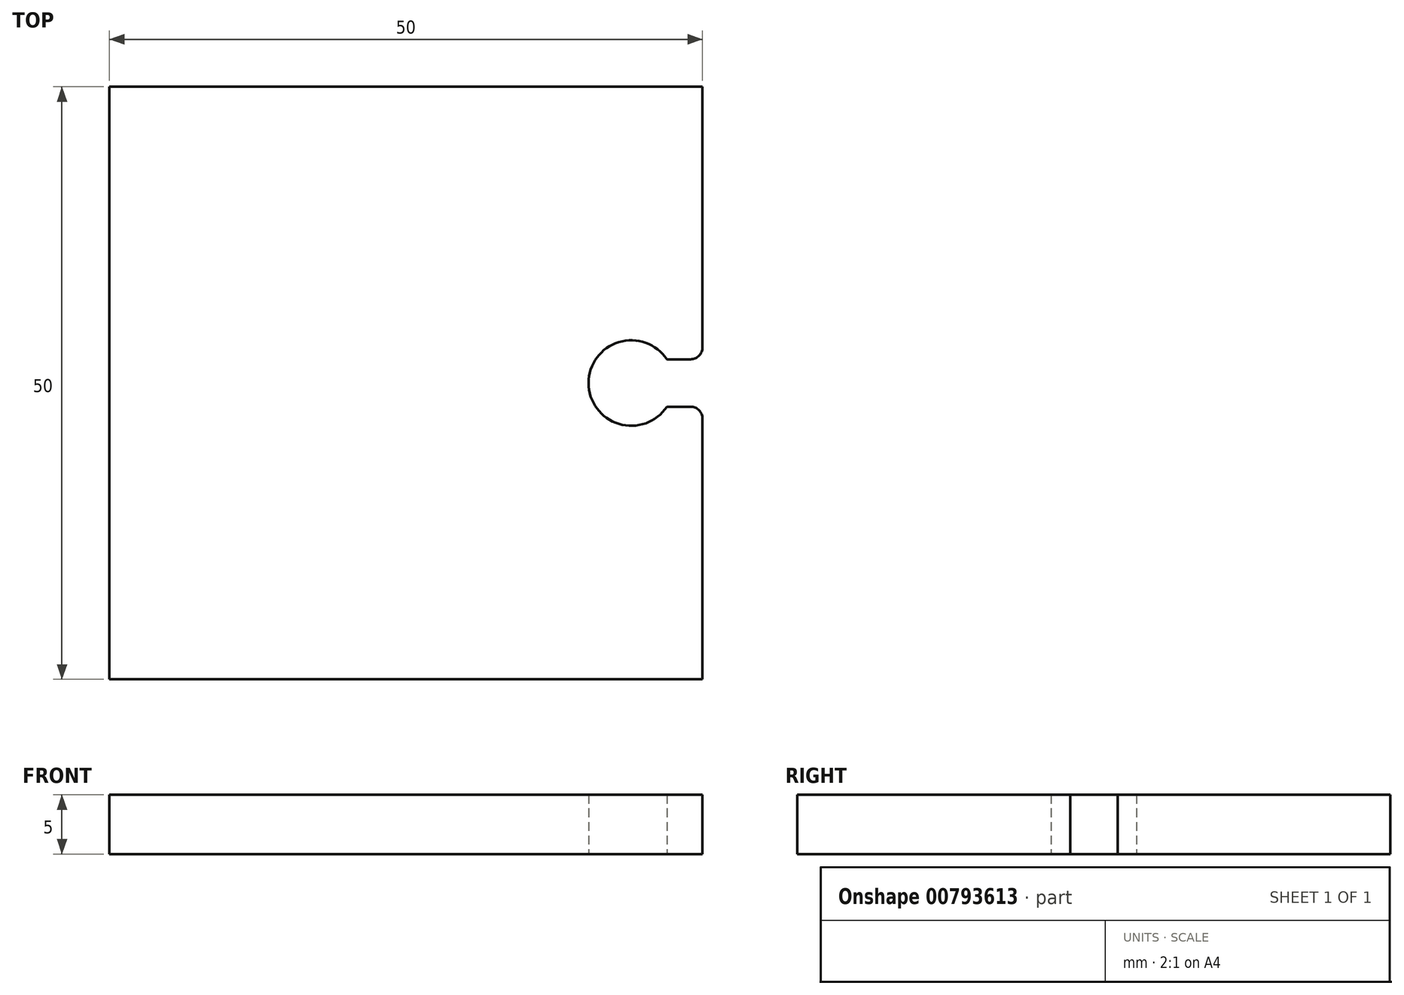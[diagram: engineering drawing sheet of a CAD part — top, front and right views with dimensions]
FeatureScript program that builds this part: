
annotation { "Feature Type Name" : "Feature", "Feature Type Description" : "" }
export const myFeature = defineFeature(function(context is Context, id is Id, definition is map)
    precondition{}
    {
        {
            var Q0;
            Q0=qCreatedBy(makeId("Top.planeOp"),FACE);
            var sketch = newSketch(context, id + "F0", { "sketchPlane" : qUnion([Q0])});
            skLineSegment(sketch, "E0.bottom", {"start": v(-25, -25) * mm, "end": v(25, -25) * mm});
            skLineSegment(sketch, "E0.top", {"start": v(-25, 25) * mm, "end": v(25, 25) * mm});
            skLineSegment(sketch, "E0.left", {"start": v(-25, -25) * mm, "end": v(-25, 25) * mm});
            skLineSegment(sketch, "E0.right", {"start": v(25, -25) * mm, "end": v(25, -3) * mm});
            skPoint(sketch, "E0.middle", {"position": v(0, 0) * mm});
            skLineSegment(sketch, "E1", {"start": v(25, 25) * mm, "end": v(25, 3) * mm});
            skLineSegment(sketch, "E2", {"start": v(24, 2) * mm, "end": v(22, 2) * mm});
            skLineSegment(sketch, "E3", {"start": v(24, -2) * mm, "end": v(22, -2) * mm});
            skArc(sketch, "E4", {"start": v(22, 2) * mm, "mid": v(15.4, 0) * mm, "end": v(22, -2) * mm});
            skLineSegment(sketch, "E5.trimOffspring", {"start": v(25, 3) * mm, "end": v(25, 25) * mm});
            skArc(sketch, "E6.filletArc", {"start": v(24, 2) * mm, "mid": v(24.7, 2.3) * mm, "end": v(25, 3) * mm});
            skArc(sketch, "E7.filletArc", {"start": v(25, -3) * mm, "mid": v(24.7, -2.3) * mm, "end": v(24, -2) * mm});
            skSolve(sketch);
        }
        {
            var Q0;
            Q0 = qSketchRegion(id + "F0", true);
            extrude(context, id + "F1", {"entities" : qUnion([Q0]), "depth" : 5 * mm, "offsetDistance" : 25 * mm});
        }
    });
